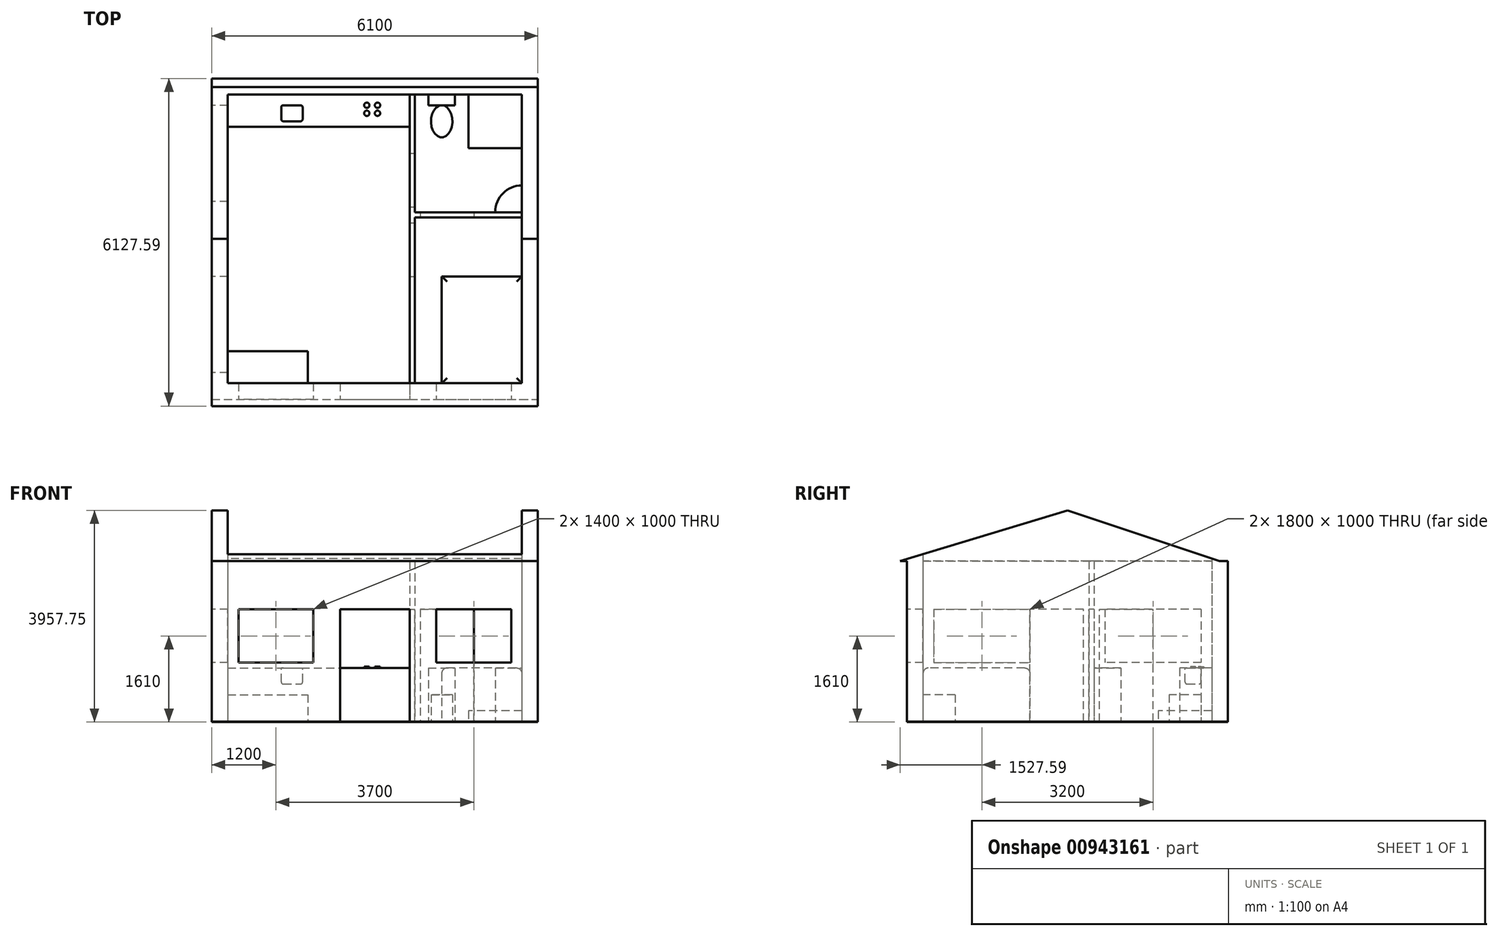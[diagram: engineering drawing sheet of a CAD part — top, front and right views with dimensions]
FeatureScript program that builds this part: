
annotation { "Feature Type Name" : "Feature", "Feature Type Description" : "" }
export const myFeature = defineFeature(function(context is Context, id is Id, definition is map)
    precondition{}
    {
        {
            var Q0;
            Q0=qCreatedBy(makeId("Top.planeOp"),FACE);
            var sketch = newSketch(context, id + "F0", { "sketchPlane" : qUnion([Q0])});
            skLineSegment(sketch, "E0", {"start": v(0, 0) * mm, "end": v(6100, 0) * mm});
            skLineSegment(sketch, "E1", {"start": v(0, 0) * mm, "end": v(0, -6000) * mm});
            skLineSegment(sketch, "E2", {"start": v(0, -6000) * mm, "end": v(6100, -6000) * mm});
            skLineSegment(sketch, "E3", {"start": v(6100, -6000) * mm, "end": v(6100, 0) * mm});
            skSolve(sketch);
        }
        {
            var Q0;
            Q0=makeQuery(id+"F0.imprint","IMPRINT",FACE,{"disambiguationData":[TD([[makeQuery(id+"F0.imprint","IMPRINT",EDGE,{"derivedFrom":sQuery(id+"F0.wireOp",EDGE,"E0")}),-1.0]])]});
            extrude(context, id + "F1", {"entities" : qUnion([Q0]), "depth" : 3000 * mm, "offsetDistance" : 25 * mm});
        }
        {
            var Q0;
            Q0=makeQuery(id+"F1.opExtrude","SWEPT_FACE",FACE,{"disambiguationData":[OSD([sQuery(id+"F0.wireOp",EDGE,"E1")])]});
            var sketch = newSketch(context, id + "F2", { "sketchPlane" : qUnion([Q0])});
            skLineSegment(sketch, "E4", {"start": v(0, 3000) * mm, "end": v(6300, 3000) * mm});
            skLineSegment(sketch, "E5", {"start": v(6300, 3000) * mm, "end": v(3000, 4000) * mm});
            skLineSegment(sketch, "E6", {"start": v(3000, 4000) * mm, "end": v(0, 3000) * mm});
            skSolve(sketch);
        }
        {
            var Q0;
            Q0 = qSketchRegion(id + "F2", true);
            extrude(context, id + "F3", {"entities" : qUnion([Q0]), "operationType" : NewBodyOperationType.ADD, "oppositeDirection" : true, "depth" : 6100 * mm, "offsetDistance" : 25 * mm});
        }
        {
            var Q0;
            Q0=makeQuery(id+"F3.boolean.opBoolean","MERGE",FACE,{"derivedFrom":[makeQuery(id+"F1.opExtrude","SWEPT_FACE",FACE,{"disambiguationData":[OSD([sQuery(id+"F0.wireOp",EDGE,"E3")])]}),makeQuery(id+"F3.opExtrude","CAP_FACE",FACE,{"disambiguationData":[OSD([sQuery(id+"F2.wireOp",EDGE,"E4"),sQuery(id+"F2.wireOp",EDGE,"E5"),sQuery(id+"F2.wireOp",EDGE,"E6")])],"isStart":false})]});
            var sketch = newSketch(context, id + "F4", { "sketchPlane" : qUnion([Q0])});
            skLineSegment(sketch, "E7", {"start": v(-6300, 3000) * mm, "end": v(-3000, 4000) * mm});
            skLineSegment(sketch, "E8", {"start": v(-3000, 4000) * mm, "end": v(0, 3000) * mm});
            skLineSegment(sketch, "E9", {"start": v(0, 3000) * mm, "end": v(-156.74, 3000) * mm});
            skLineSegment(sketch, "E10", {"start": v(-156.74, 3000) * mm, "end": v(-3000, 3947.75) * mm});
            skLineSegment(sketch, "E11", {"start": v(-3000, 3947.75) * mm, "end": v(-6127.6, 3000) * mm});
            skLineSegment(sketch, "E12", {"start": v(-6127.6, 3000) * mm, "end": v(-6300, 3000) * mm});
            skSolve(sketch);
        }
        {
            var Q0;
            Q0 = qSketchRegion(id + "F4", true);
            extrude(context, id + "F5", {"entities" : qUnion([Q0]), "operationType" : NewBodyOperationType.REMOVE, "oppositeDirection" : true, "depth" : 6100 * mm, "offsetDistance" : 25 * mm});
        }
        {
            var Q0;
            Q0=makeQuery(id+"F1.opExtrude","CAP_FACE",FACE,{"disambiguationData":[OSD([sQuery(id+"F0.wireOp",EDGE,"E0"),sQuery(id+"F0.wireOp",EDGE,"E1"),sQuery(id+"F0.wireOp",EDGE,"E2"),sQuery(id+"F0.wireOp",EDGE,"E3")])],"isStart":true});
            var sketch = newSketch(context, id + "F6", { "sketchPlane" : qUnion([Q0])});
            skLineSegment(sketch, "E13.bottom", {"start": v(300, 300) * mm, "end": v(5800, 300) * mm});
            skLineSegment(sketch, "E13.top", {"start": v(300, 5700) * mm, "end": v(5800, 5700) * mm});
            skLineSegment(sketch, "E13.left", {"start": v(300, 300) * mm, "end": v(300, 5700) * mm});
            skLineSegment(sketch, "E13.right", {"start": v(5800, 300) * mm, "end": v(5800, 5700) * mm});
            skSolve(sketch);
        }
        {
            var Q0;
            Q0 = qSketchRegion(id + "F6", true);
            extrude(context, id + "F7", {"entities" : qUnion([Q0]), "operationType" : NewBodyOperationType.REMOVE, "endBound" : BoundingType.THROUGH_ALL, "oppositeDirection" : true, "depth" : 25 * mm, "offsetDistance" : 25 * mm});
        }
        {
            var Q0;
            Q0=makeQuery(id+"F1.opExtrude","SWEPT_FACE",FACE,{"disambiguationData":[OSD([sQuery(id+"F0.wireOp",EDGE,"E2")])]});
            var sketch = newSketch(context, id + "F8", { "sketchPlane" : qUnion([Q0])});
            skLineSegment(sketch, "E14.bottom", {"start": v(2400, 0) * mm, "end": v(3700, 0) * mm});
            skLineSegment(sketch, "E14.top", {"start": v(2400, 2100) * mm, "end": v(3700, 2100) * mm});
            skLineSegment(sketch, "E14.left", {"start": v(2400, 0) * mm, "end": v(2400, 2100) * mm});
            skLineSegment(sketch, "E14.right", {"start": v(3700, 0) * mm, "end": v(3700, 2100) * mm});
            skLineSegment(sketch, "E15", {"start": v(3700, 2100) * mm, "end": v(4200, 2100) * mm, "construction": true});
            skLineSegment(sketch, "E16.bottom", {"start": v(4200, 2100) * mm, "end": v(5600, 2100) * mm});
            skLineSegment(sketch, "E16.top", {"start": v(4200, 1100) * mm, "end": v(5600, 1100) * mm});
            skLineSegment(sketch, "E16.left", {"start": v(4200, 2100) * mm, "end": v(4200, 1100) * mm});
            skLineSegment(sketch, "E16.right", {"start": v(5600, 2100) * mm, "end": v(5600, 1100) * mm});
            skLineSegment(sketch, "E17", {"start": v(2400, 2100) * mm, "end": v(1900, 2100) * mm, "construction": true});
            skLineSegment(sketch, "E18.bottom", {"start": v(1900, 2100) * mm, "end": v(500, 2100) * mm});
            skLineSegment(sketch, "E18.top", {"start": v(1900, 1100) * mm, "end": v(500, 1100) * mm});
            skLineSegment(sketch, "E18.left", {"start": v(1900, 2100) * mm, "end": v(1900, 1100) * mm});
            skLineSegment(sketch, "E18.right", {"start": v(500, 2100) * mm, "end": v(500, 1100) * mm});
            skSolve(sketch);
        }
        {
            var Q0;
            Q0 = qSketchRegion(id + "F8", true);
            extrude(context, id + "F9", {"entities" : qUnion([Q0]), "operationType" : NewBodyOperationType.REMOVE, "oppositeDirection" : true, "depth" : 1000 * mm, "offsetDistance" : 25 * mm});
        }
        {
            var Q0;
            Q0=makeQuery(id+"F1.opExtrude","CAP_FACE",FACE,{"disambiguationData":[OSD([sQuery(id+"F0.wireOp",EDGE,"E0"),sQuery(id+"F0.wireOp",EDGE,"E1"),sQuery(id+"F0.wireOp",EDGE,"E2"),sQuery(id+"F0.wireOp",EDGE,"E3")])],"isStart":true});
            var sketch = newSketch(context, id + "F10", { "sketchPlane" : qUnion([Q0])});
            skLineSegment(sketch, "E19.bottom", {"start": v(5800, 5700) * mm, "end": v(4300, 5700) * mm});
            skLineSegment(sketch, "E19.top", {"start": v(5800, 3700) * mm, "end": v(4300, 3700) * mm});
            skLineSegment(sketch, "E19.left", {"start": v(5800, 5700) * mm, "end": v(5800, 3700) * mm});
            skLineSegment(sketch, "E19.right", {"start": v(4300, 5700) * mm, "end": v(4300, 3700) * mm});
            skSolve(sketch);
        }
        {
            var Q0;
            Q0 = qSketchRegion(id + "F10", true);
            extrude(context, id + "F11", {"entities" : qUnion([Q0]), "oppositeDirection" : true, "depth" : 1000 * mm, "offsetDistance" : 25 * mm});
        }
        {
            var Q0;
            Q0=makeQuery(id+"F11.opExtrude","CAP_FACE",FACE,{"disambiguationData":[OSD([sQuery(id+"F10.wireOp",EDGE,"E19.bottom"),sQuery(id+"F10.wireOp",EDGE,"E19.top"),sQuery(id+"F10.wireOp",EDGE,"E19.left"),sQuery(id+"F10.wireOp",EDGE,"E19.right")])],"isStart":true});
            var sketch = newSketch(context, id + "F12", { "sketchPlane" : qUnion([Q0])});
            skLineSegment(sketch, "E20.bottom", {"start": v(5800, 300) * mm, "end": v(4800, 300) * mm});
            skLineSegment(sketch, "E20.top", {"start": v(5800, 1300) * mm, "end": v(4800, 1300) * mm});
            skLineSegment(sketch, "E20.left", {"start": v(5800, 300) * mm, "end": v(5800, 1300) * mm});
            skLineSegment(sketch, "E20.right", {"start": v(4800, 300) * mm, "end": v(4800, 1300) * mm});
            skSolve(sketch);
        }
        {
            var Q0;
            Q0 = qSketchRegion(id + "F12", true);
            extrude(context, id + "F13", {"entities" : qUnion([Q0]), "oppositeDirection" : true, "depth" : 200 * mm, "offsetDistance" : 25 * mm});
        }
        {
            var Q0;
            Q0=makeQuery(id+"F1.opExtrude","CAP_FACE",FACE,{"disambiguationData":[OSD([sQuery(id+"F0.wireOp",EDGE,"E0"),sQuery(id+"F0.wireOp",EDGE,"E1"),sQuery(id+"F0.wireOp",EDGE,"E2"),sQuery(id+"F0.wireOp",EDGE,"E3")])],"isStart":true});
            var sketch = newSketch(context, id + "F14", { "sketchPlane" : qUnion([Q0])});
            skLineSegment(sketch, "E21.bottom", {"start": v(3700, 5700) * mm, "end": v(3800, 5700) * mm});
            skLineSegment(sketch, "E21.top", {"start": v(3700, 300) * mm, "end": v(3800, 300) * mm});
            skLineSegment(sketch, "E21.left", {"start": v(3700, 5700) * mm, "end": v(3700, 300) * mm});
            skLineSegment(sketch, "E21.right", {"start": v(3800, 5700) * mm, "end": v(3800, 300) * mm, "construction": true});
            skLineSegment(sketch, "E22", {"start": v(3800, 300) * mm, "end": v(3800, 2500) * mm});
            skLineSegment(sketch, "E23", {"start": v(3800, 2500) * mm, "end": v(5800, 2500) * mm});
            skLineSegment(sketch, "E24", {"start": v(5800, 2500) * mm, "end": v(5800, 2600) * mm});
            skLineSegment(sketch, "E25", {"start": v(5800, 2600) * mm, "end": v(3800, 2600) * mm});
            skLineSegment(sketch, "E26", {"start": v(3800, 2600) * mm, "end": v(3800, 5700) * mm});
            skSolve(sketch);
        }
        {
            var Q0;
            Q0 = qSketchRegion(id + "F14", true);
            extrude(context, id + "F15", {"entities" : qUnion([Q0]), "operationType" : NewBodyOperationType.ADD, "oppositeDirection" : true, "depth" : 3000 * mm, "offsetDistance" : 25 * mm});
        }
        {
            var Q0;
            Q0=makeQuery(id+"F3.boolean.opBoolean","MERGE",FACE,{"derivedFrom":[makeQuery(id+"F1.opExtrude","SWEPT_FACE",FACE,{"disambiguationData":[OSD([sQuery(id+"F0.wireOp",EDGE,"E1")])]}),makeQuery(id+"F3.opExtrude","CAP_FACE",FACE,{"disambiguationData":[OSD([sQuery(id+"F2.wireOp",EDGE,"E4"),sQuery(id+"F2.wireOp",EDGE,"E5"),sQuery(id+"F2.wireOp",EDGE,"E6")])],"isStart":true})]});
            var sketch = newSketch(context, id + "F16", { "sketchPlane" : qUnion([Q0])});
            skLineSegment(sketch, "E27", {"start": v(500, 2100) * mm, "end": v(5500, 2100) * mm, "construction": true});
            skLineSegment(sketch, "E28.bottom", {"start": v(5500, 2100) * mm, "end": v(3700, 2100) * mm});
            skLineSegment(sketch, "E28.top", {"start": v(5500, 1100) * mm, "end": v(3700, 1100) * mm});
            skLineSegment(sketch, "E28.left", {"start": v(5500, 2100) * mm, "end": v(5500, 1100) * mm});
            skLineSegment(sketch, "E28.right", {"start": v(3700, 2100) * mm, "end": v(3700, 1100) * mm});
            skLineSegment(sketch, "E29.bottom", {"start": v(500, 2100) * mm, "end": v(2300, 2100) * mm});
            skLineSegment(sketch, "E29.top", {"start": v(500, 1100) * mm, "end": v(2300, 1100) * mm});
            skLineSegment(sketch, "E29.left", {"start": v(500, 2100) * mm, "end": v(500, 1100) * mm});
            skLineSegment(sketch, "E29.right", {"start": v(2300, 2100) * mm, "end": v(2300, 1100) * mm});
            skSolve(sketch);
        }
        {
            var Q0;
            Q0 = qSketchRegion(id + "F16", true);
            extrude(context, id + "F17", {"entities" : qUnion([Q0]), "operationType" : NewBodyOperationType.REMOVE, "oppositeDirection" : true, "depth" : 1000 * mm, "offsetDistance" : 25 * mm});
        }
        {
            var Q0;
            Q0=makeQuery(id+"F15.boolean.opBoolean","MERGE",FACE,{"derivedFrom":[makeQuery(id+"F1.opExtrude","CAP_FACE",FACE,{"disambiguationData":[OSD([sQuery(id+"F0.wireOp",EDGE,"E0"),sQuery(id+"F0.wireOp",EDGE,"E1"),sQuery(id+"F0.wireOp",EDGE,"E2"),sQuery(id+"F0.wireOp",EDGE,"E3")])],"isStart":true}),makeQuery(id+"F15.opExtrude","CAP_FACE",FACE,{"disambiguationData":[OSD([sQuery(id+"F14.wireOp",EDGE,"E21.bottom"),sQuery(id+"F14.wireOp",EDGE,"E21.top"),sQuery(id+"F14.wireOp",EDGE,"E21.left"),sQuery(id+"F14.wireOp",EDGE,"E22"),sQuery(id+"F14.wireOp",EDGE,"E23"),sQuery(id+"F14.wireOp",EDGE,"E24"),sQuery(id+"F14.wireOp",EDGE,"E25"),sQuery(id+"F14.wireOp",EDGE,"E26")])],"isStart":true})]});
            var sketch = newSketch(context, id + "F18", { "sketchPlane" : qUnion([Q0])});
            skEllipse(sketch, "E30", {"center": v(4300, 800) * mm, "majorRadius": 300 * mm, "minorRadius": 200 * mm, "majorAxis": v(0, -1)});
            skSolve(sketch);
        }
        {
            var Q0;
            Q0 = qSketchRegion(id + "F18", true);
            extrude(context, id + "F19", {"entities" : qUnion([Q0]), "oppositeDirection" : true, "depth" : 500 * mm, "offsetDistance" : 25 * mm});
        }
        {
            var Q0;
            Q0=makeQuery(id+"F15.boolean.opBoolean","MERGE",FACE,{"derivedFrom":[makeQuery(id+"F1.opExtrude","CAP_FACE",FACE,{"disambiguationData":[OSD([sQuery(id+"F0.wireOp",EDGE,"E0"),sQuery(id+"F0.wireOp",EDGE,"E1"),sQuery(id+"F0.wireOp",EDGE,"E2"),sQuery(id+"F0.wireOp",EDGE,"E3")])],"isStart":true}),makeQuery(id+"F15.opExtrude","CAP_FACE",FACE,{"disambiguationData":[OSD([sQuery(id+"F14.wireOp",EDGE,"E21.bottom"),sQuery(id+"F14.wireOp",EDGE,"E21.top"),sQuery(id+"F14.wireOp",EDGE,"E21.left"),sQuery(id+"F14.wireOp",EDGE,"E22"),sQuery(id+"F14.wireOp",EDGE,"E23"),sQuery(id+"F14.wireOp",EDGE,"E24"),sQuery(id+"F14.wireOp",EDGE,"E25"),sQuery(id+"F14.wireOp",EDGE,"E26")])],"isStart":true})]});
            var sketch = newSketch(context, id + "F20", { "sketchPlane" : qUnion([Q0])});
            skLineSegment(sketch, "E31.bottom", {"start": v(4050, 300) * mm, "end": v(4550, 300) * mm});
            skLineSegment(sketch, "E31.top", {"start": v(4050, 500) * mm, "end": v(4550, 500) * mm});
            skLineSegment(sketch, "E31.left", {"start": v(4050, 300) * mm, "end": v(4050, 500) * mm});
            skLineSegment(sketch, "E31.right", {"start": v(4550, 300) * mm, "end": v(4550, 500) * mm});
            skSolve(sketch);
        }
        {
            var Q0;
            Q0 = qSketchRegion(id + "F20", true);
            extrude(context, id + "F21", {"entities" : qUnion([Q0]), "oppositeDirection" : true, "depth" : 1000 * mm, "offsetDistance" : 25 * mm});
        }
        {
            var Q0;
            Q0=makeQuery(id+"F15.boolean.opBoolean","MERGE",FACE,{"derivedFrom":[makeQuery(id+"F1.opExtrude","CAP_FACE",FACE,{"disambiguationData":[OSD([sQuery(id+"F0.wireOp",EDGE,"E0"),sQuery(id+"F0.wireOp",EDGE,"E1"),sQuery(id+"F0.wireOp",EDGE,"E2"),sQuery(id+"F0.wireOp",EDGE,"E3")])],"isStart":true}),makeQuery(id+"F15.opExtrude","CAP_FACE",FACE,{"disambiguationData":[OSD([sQuery(id+"F14.wireOp",EDGE,"E21.bottom"),sQuery(id+"F14.wireOp",EDGE,"E21.top"),sQuery(id+"F14.wireOp",EDGE,"E21.left"),sQuery(id+"F14.wireOp",EDGE,"E22"),sQuery(id+"F14.wireOp",EDGE,"E23"),sQuery(id+"F14.wireOp",EDGE,"E24"),sQuery(id+"F14.wireOp",EDGE,"E25"),sQuery(id+"F14.wireOp",EDGE,"E26")])],"isStart":true})]});
            var sketch = newSketch(context, id + "F22", { "sketchPlane" : qUnion([Q0])});
            skLineSegment(sketch, "E32", {"start": v(5800, 2500) * mm, "end": v(5800, 2000) * mm});
            skLineSegment(sketch, "E33", {"start": v(5800, 2500) * mm, "end": v(5300, 2500) * mm});
            skArc(sketch, "E34", {"start": v(5300, 2500) * mm, "mid": v(5446.45, 2146.45) * mm, "end": v(5800, 2000) * mm});
            skSolve(sketch);
        }
        {
            var Q0;
            Q0 = qSketchRegion(id + "F22", true);
            extrude(context, id + "F23", {"entities" : qUnion([Q0]), "oppositeDirection" : true, "depth" : 1000 * mm, "offsetDistance" : 25 * mm});
        }
        {
            var Q0;
            Q0=makeQuery(id+"F15.opExtrude","SWEPT_FACE",FACE,{"disambiguationData":[OSD([sQuery(id+"F14.wireOp",EDGE,"E22")])]});
            var sketch = newSketch(context, id + "F24", { "sketchPlane" : qUnion([Q0])});
            skLineSegment(sketch, "E35.bottom", {"start": v(-2400, 0) * mm, "end": v(-1400, 0) * mm});
            skLineSegment(sketch, "E35.top", {"start": v(-2400, 2100) * mm, "end": v(-1400, 2100) * mm});
            skLineSegment(sketch, "E35.left", {"start": v(-2400, 0) * mm, "end": v(-2400, 2100) * mm});
            skLineSegment(sketch, "E35.right", {"start": v(-1400, 0) * mm, "end": v(-1400, 2100) * mm});
            skLineSegment(sketch, "E36.bottom", {"start": v(-2700, 0) * mm, "end": v(-3700, 0) * mm});
            skLineSegment(sketch, "E36.top", {"start": v(-2700, 2100) * mm, "end": v(-3700, 2100) * mm});
            skLineSegment(sketch, "E36.left", {"start": v(-2700, 0) * mm, "end": v(-2700, 2100) * mm});
            skLineSegment(sketch, "E36.right", {"start": v(-3700, 0) * mm, "end": v(-3700, 2100) * mm});
            skSolve(sketch);
        }
        {
            var Q0;
            Q0 = qSketchRegion(id + "F24", true);
            extrude(context, id + "F25", {"entities" : qUnion([Q0]), "operationType" : NewBodyOperationType.REMOVE, "oppositeDirection" : true, "depth" : 500 * mm, "offsetDistance" : 25 * mm});
        }
        {
            var Q0;
            Q0=makeQuery(id+"F15.boolean.opBoolean","MERGE",FACE,{"derivedFrom":[makeQuery(id+"F1.opExtrude","CAP_FACE",FACE,{"disambiguationData":[OSD([sQuery(id+"F0.wireOp",EDGE,"E0"),sQuery(id+"F0.wireOp",EDGE,"E1"),sQuery(id+"F0.wireOp",EDGE,"E2"),sQuery(id+"F0.wireOp",EDGE,"E3")])],"isStart":true}),makeQuery(id+"F15.opExtrude","CAP_FACE",FACE,{"disambiguationData":[OSD([sQuery(id+"F14.wireOp",EDGE,"E21.bottom"),sQuery(id+"F14.wireOp",EDGE,"E21.top"),sQuery(id+"F14.wireOp",EDGE,"E21.left"),sQuery(id+"F14.wireOp",EDGE,"E22"),sQuery(id+"F14.wireOp",EDGE,"E23"),sQuery(id+"F14.wireOp",EDGE,"E24"),sQuery(id+"F14.wireOp",EDGE,"E25"),sQuery(id+"F14.wireOp",EDGE,"E26")])],"isStart":true})]});
            var sketch = newSketch(context, id + "F26", { "sketchPlane" : qUnion([Q0])});
            skLineSegment(sketch, "E37.bottom", {"start": v(300, 300) * mm, "end": v(3700, 300) * mm});
            skLineSegment(sketch, "E37.top", {"start": v(300, 900) * mm, "end": v(3700, 900) * mm});
            skLineSegment(sketch, "E37.left", {"start": v(300, 300) * mm, "end": v(300, 900) * mm});
            skLineSegment(sketch, "E37.right", {"start": v(3700, 300) * mm, "end": v(3700, 900) * mm});
            skSolve(sketch);
        }
        {
            var Q0;
            Q0 = qSketchRegion(id + "F26", true);
            extrude(context, id + "F27", {"entities" : qUnion([Q0]), "oppositeDirection" : true, "depth" : 1000 * mm, "offsetDistance" : 25 * mm});
        }
        {
            var Q0;
            Q0=makeQuery(id+"F27.opExtrude","CAP_FACE",FACE,{"disambiguationData":[OSD([sQuery(id+"F26.wireOp",EDGE,"E37.bottom"),sQuery(id+"F26.wireOp",EDGE,"E37.top"),sQuery(id+"F26.wireOp",EDGE,"E37.left"),sQuery(id+"F26.wireOp",EDGE,"E37.right")])],"isStart":false});
            var sketch = newSketch(context, id + "F28", { "sketchPlane" : qUnion([Q0])});
            skLineSegment(sketch, "E38.bottom", {"start": v(1300, -800) * mm, "end": v(1700, -800) * mm});
            skLineSegment(sketch, "E38.top", {"start": v(1300, -500) * mm, "end": v(1700, -500) * mm});
            skLineSegment(sketch, "E38.left", {"start": v(1300, -800) * mm, "end": v(1300, -500) * mm});
            skLineSegment(sketch, "E38.right", {"start": v(1700, -800) * mm, "end": v(1700, -500) * mm});
            skSolve(sketch);
        }
        {
            var Q0;
            Q0 = qSketchRegion(id + "F28", true);
            extrude(context, id + "F29", {"entities" : qUnion([Q0]), "operationType" : NewBodyOperationType.REMOVE, "oppositeDirection" : true, "depth" : 300 * mm, "offsetDistance" : 25 * mm});
        }
        {
            var Q0;
            Q0=makeQuery(id+"F15.opExtrude","SWEPT_FACE",FACE,{"disambiguationData":[OSD([sQuery(id+"F14.wireOp",EDGE,"E25")])]});
            var sketch = newSketch(context, id + "F30", { "sketchPlane" : qUnion([Q0])});
            skLineSegment(sketch, "E39.bottom", {"start": v(3900, 0) * mm, "end": v(4900, 0) * mm});
            skLineSegment(sketch, "E39.top", {"start": v(3900, 2100) * mm, "end": v(4900, 2100) * mm});
            skLineSegment(sketch, "E39.left", {"start": v(3900, 0) * mm, "end": v(3900, 2100) * mm});
            skLineSegment(sketch, "E39.right", {"start": v(4900, 0) * mm, "end": v(4900, 2100) * mm});
            skSolve(sketch);
        }
        {
            var Q0;
            Q0 = qSketchRegion(id + "F30", true);
            extrude(context, id + "F31", {"entities" : qUnion([Q0]), "operationType" : NewBodyOperationType.REMOVE, "oppositeDirection" : true, "depth" : 500 * mm, "offsetDistance" : 25 * mm});
        }
        {
            var Q0;
            Q0=makeQuery(id+"F29.boolean.opBoolean","COPY",EDGE,{"derivedFrom":makeQuery(id+"F29.opExtrude","SWEPT_EDGE",EDGE,{"disambiguationData":[OSD([sQuery(id+"F28.wireOp",EDGE,"E38.top"),sQuery(id+"F28.wireOp",EDGE,"E38.right")])]})});
            var Q1;
            Q1=makeQuery(id+"F29.boolean.opBoolean","COPY",EDGE,{"derivedFrom":makeQuery(id+"F29.opExtrude","SWEPT_EDGE",EDGE,{"disambiguationData":[OSD([sQuery(id+"F28.wireOp",EDGE,"E38.top"),sQuery(id+"F28.wireOp",EDGE,"E38.left")])]})});
            var Q2;
            Q2=makeQuery(id+"F29.boolean.opBoolean","COPY",EDGE,{"derivedFrom":makeQuery(id+"F29.opExtrude","SWEPT_EDGE",EDGE,{"disambiguationData":[OSD([sQuery(id+"F28.wireOp",EDGE,"E38.bottom"),sQuery(id+"F28.wireOp",EDGE,"E38.left")])]})});
            var Q3;
            Q3=makeQuery(id+"F29.boolean.opBoolean","COPY",EDGE,{"derivedFrom":makeQuery(id+"F29.opExtrude","CAP_EDGE",EDGE,{"disambiguationData":[OSD([sQuery(id+"F28.wireOp",EDGE,"E38.top")])],"isStart":false})});
            var Q4;
            Q4=makeQuery(id+"F29.boolean.opBoolean","COPY",EDGE,{"derivedFrom":makeQuery(id+"F29.opExtrude","CAP_EDGE",EDGE,{"disambiguationData":[OSD([sQuery(id+"F28.wireOp",EDGE,"E38.right")])],"isStart":false})});
            var Q5;
            Q5=makeQuery(id+"F29.boolean.opBoolean","COPY",EDGE,{"derivedFrom":makeQuery(id+"F29.opExtrude","CAP_EDGE",EDGE,{"disambiguationData":[OSD([sQuery(id+"F28.wireOp",EDGE,"E38.left")])],"isStart":false})});
            var Q6;
            Q6=makeQuery(id+"F29.boolean.opBoolean","COPY",EDGE,{"derivedFrom":makeQuery(id+"F29.opExtrude","CAP_EDGE",EDGE,{"disambiguationData":[OSD([sQuery(id+"F28.wireOp",EDGE,"E38.bottom")])],"isStart":false})});
            var Q7;
            Q7=makeQuery(id+"F29.boolean.opBoolean","COPY",EDGE,{"derivedFrom":makeQuery(id+"F29.opExtrude","SWEPT_EDGE",EDGE,{"disambiguationData":[OSD([sQuery(id+"F28.wireOp",EDGE,"E38.bottom"),sQuery(id+"F28.wireOp",EDGE,"E38.right")])]})});
            fillet(context, id + "F32", {"entities" : qUnion([Q0, Q1, Q2, Q3, Q4, Q5, Q6, Q7]), "radius" : 40 * mm, "tangentPropagation" : true, "allowEdgeOverflow" : false});
        }
        {
            var Q0;
            Q0=makeQuery(id+"F11.opExtrude","CAP_FACE",FACE,{"disambiguationData":[OSD([sQuery(id+"F10.wireOp",EDGE,"E19.bottom"),sQuery(id+"F10.wireOp",EDGE,"E19.top"),sQuery(id+"F10.wireOp",EDGE,"E19.left"),sQuery(id+"F10.wireOp",EDGE,"E19.right")])],"isStart":false});
            fillet(context, id + "F33", {"entities" : qUnion([Q0]), "radius" : 100 * mm, "tangentPropagation" : true, "allowEdgeOverflow" : false});
        }
        {
            var Q0;
            {var subQ3=sQuery(id+"F0.wireOp",EDGE,"E3");var subQ4=sQuery(id+"F0.wireOp",EDGE,"E0");var subQ5=sQuery(id+"F14.wireOp",EDGE,"E22");var subQ6=sQuery(id+"F0.wireOp",EDGE,"E1");var subQ7=sQuery(id+"F14.wireOp",EDGE,"E25");var subQ8=sQuery(id+"F0.wireOp",EDGE,"E2");var subQ9=sQuery(id+"F14.wireOp",EDGE,"E26");var subQ10=sQuery(id+"F14.wireOp",EDGE,"E21.left");var subQ11=sQuery(id+"F14.wireOp",EDGE,"E23");Q0=makeQuery(id+"F31.boolean.opBoolean","SPLIT",FACE,{"disambiguationData":[TD([makeQuery(id+"F1.opExtrude","SWEPT_FACE",FACE,{"disambiguationData":[OSD([subQ4])]})])],"derivedFrom":makeQuery(id+"F15.boolean.opBoolean","MERGE",FACE,{"derivedFrom":[makeQuery(id+"F1.opExtrude","CAP_FACE",FACE,{"disambiguationData":[OSD([subQ4,subQ6,subQ8,subQ3])],"isStart":true}),makeQuery(id+"F15.opExtrude","CAP_FACE",FACE,{"disambiguationData":[OSD([sQuery(id+"F14.wireOp",EDGE,"E21.bottom"),sQuery(id+"F14.wireOp",EDGE,"E21.top"),subQ10,subQ5,subQ11,sQuery(id+"F14.wireOp",EDGE,"E24"),subQ7,subQ9])],"isStart":true})]})});}
            var sketch = newSketch(context, id + "F34", { "sketchPlane" : qUnion([Q0])});
            skLineSegment(sketch, "E40.bottom", {"start": v(0, 0) * mm, "end": v(6100, 0) * mm});
            skLineSegment(sketch, "E40.top", {"start": v(0, 6000) * mm, "end": v(6100, 6000) * mm});
            skLineSegment(sketch, "E40.left", {"start": v(0, 0) * mm, "end": v(0, 6000) * mm});
            skLineSegment(sketch, "E40.right", {"start": v(6100, 0) * mm, "end": v(6100, 6000) * mm});
            skSolve(sketch);
        }
        {
            var Q0;
            Q0 = qSketchRegion(id + "F34", true);
            extrude(context, id + "F35", {"entities" : qUnion([Q0]), "depth" : 10 * mm, "offsetDistance" : 25 * mm});
        }
        {
            var Q0;
            Q0=makeQuery(id+"F27.opExtrude","CAP_FACE",FACE,{"disambiguationData":[OSD([sQuery(id+"F26.wireOp",EDGE,"E37.bottom"),sQuery(id+"F26.wireOp",EDGE,"E37.top"),sQuery(id+"F26.wireOp",EDGE,"E37.left"),sQuery(id+"F26.wireOp",EDGE,"E37.right")])],"isStart":false});
            var sketch = newSketch(context, id + "F36", { "sketchPlane" : qUnion([Q0])});
            skLineSegment(sketch, "E41.bottom", {"start": v(2900, -500) * mm, "end": v(3100, -500) * mm, "construction": true});
            skLineSegment(sketch, "E41.top", {"start": v(2900, -650) * mm, "end": v(3100, -650) * mm, "construction": true});
            skLineSegment(sketch, "E41.left", {"start": v(2900, -500) * mm, "end": v(2900, -650) * mm, "construction": true});
            skLineSegment(sketch, "E41.right", {"start": v(3100, -500) * mm, "end": v(3100, -650) * mm, "construction": true});
            skCircle(sketch, "E42", {"center": v(2900, -650) * mm, "radius": 50 * mm});
            skCircle(sketch, "E43", {"center": v(3100, -650) * mm, "radius": 50 * mm});
            skCircle(sketch, "E44", {"center": v(3100, -500) * mm, "radius": 50 * mm});
            skCircle(sketch, "E45", {"center": v(2900, -500) * mm, "radius": 50 * mm});
            skSolve(sketch);
        }
        {
            var Q0;
            Q0 = qSketchRegion(id + "F36", true);
            extrude(context, id + "F37", {"entities" : qUnion([Q0]), "operationType" : NewBodyOperationType.ADD, "depth" : 25 * mm, "offsetDistance" : 25 * mm});
        }
        {
            var Q0;
            Q0=makeQuery(id+"F35.opExtrude","CAP_FACE",FACE,{"disambiguationData":[OSD([sQuery(id+"F34.wireOp",EDGE,"E40.bottom"),sQuery(id+"F34.wireOp",EDGE,"E40.top"),sQuery(id+"F34.wireOp",EDGE,"E40.left"),sQuery(id+"F34.wireOp",EDGE,"E40.right")])],"isStart":true});
            var sketch = newSketch(context, id + "F38", { "sketchPlane" : qUnion([Q0])});
            skLineSegment(sketch, "E46", {"start": v(300, -5100) * mm, "end": v(300, -5700) * mm});
            skLineSegment(sketch, "E47", {"start": v(300, -5700) * mm, "end": v(1800, -5700) * mm});
            skLineSegment(sketch, "E48", {"start": v(300, -5100) * mm, "end": v(1800, -5100) * mm});
            skLineSegment(sketch, "E49", {"start": v(1800, -5100) * mm, "end": v(1800, -5700) * mm});
            skSolve(sketch);
        }
        {
            var Q0;
            Q0 = qSketchRegion(id + "F38", true);
            extrude(context, id + "F39", {"entities" : qUnion([Q0]), "depth" : 500 * mm, "offsetDistance" : 25 * mm});
        }
    });
